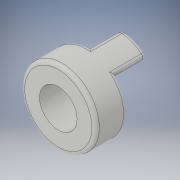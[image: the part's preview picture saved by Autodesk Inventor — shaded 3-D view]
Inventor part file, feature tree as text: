
AUTODESK INVENTOR PART (.ipt)
format: ipt  version: 2018 (Build 220112000, 112)  size: 210,432 bytes
history: native  units: in
note: dims shown in document units (in); Inventor stores cm internally (conversion verified against a paired STEP export)
features: extrude x2, fillet x2, sketch x1, pattern_circular x1
ambient origin geometry x8: Origin, YZ Plane, XZ Plane, XY Plane, X Axis, Y Axis, Z Axis, Center Point
bodies: Solid1 (feature_tree)
feature tree (6):
  sketch  "Sketch1"  dims[d0=0.625in d2=45.0deg d4=0.2656in d5=0.0in d6=0.2656in d7=0.0in d8=0.0312in d9=0.7874in d10=360.0deg d12=0.0312in d13=0.315in d14=0.1375in]
  extrude  "Extrusion1"  TaperAngle=45.0deg  [1 undecoded]
  extrude  "Extrusion2"  Depth=0.2656in TaperAngle=0.0deg
  fillet  "Fillet1"  Radius=0.2656in
  pattern_circular  "Circular Pattern1"  [2 undecoded]
  fillet  "Fillet2"  Radius=0.7874in
note: 3 required parameter values undecoded (feature->parameter linkage not recoverable at this tier; creation-order binding heuristic only, values carry confidence <= 0.55)
